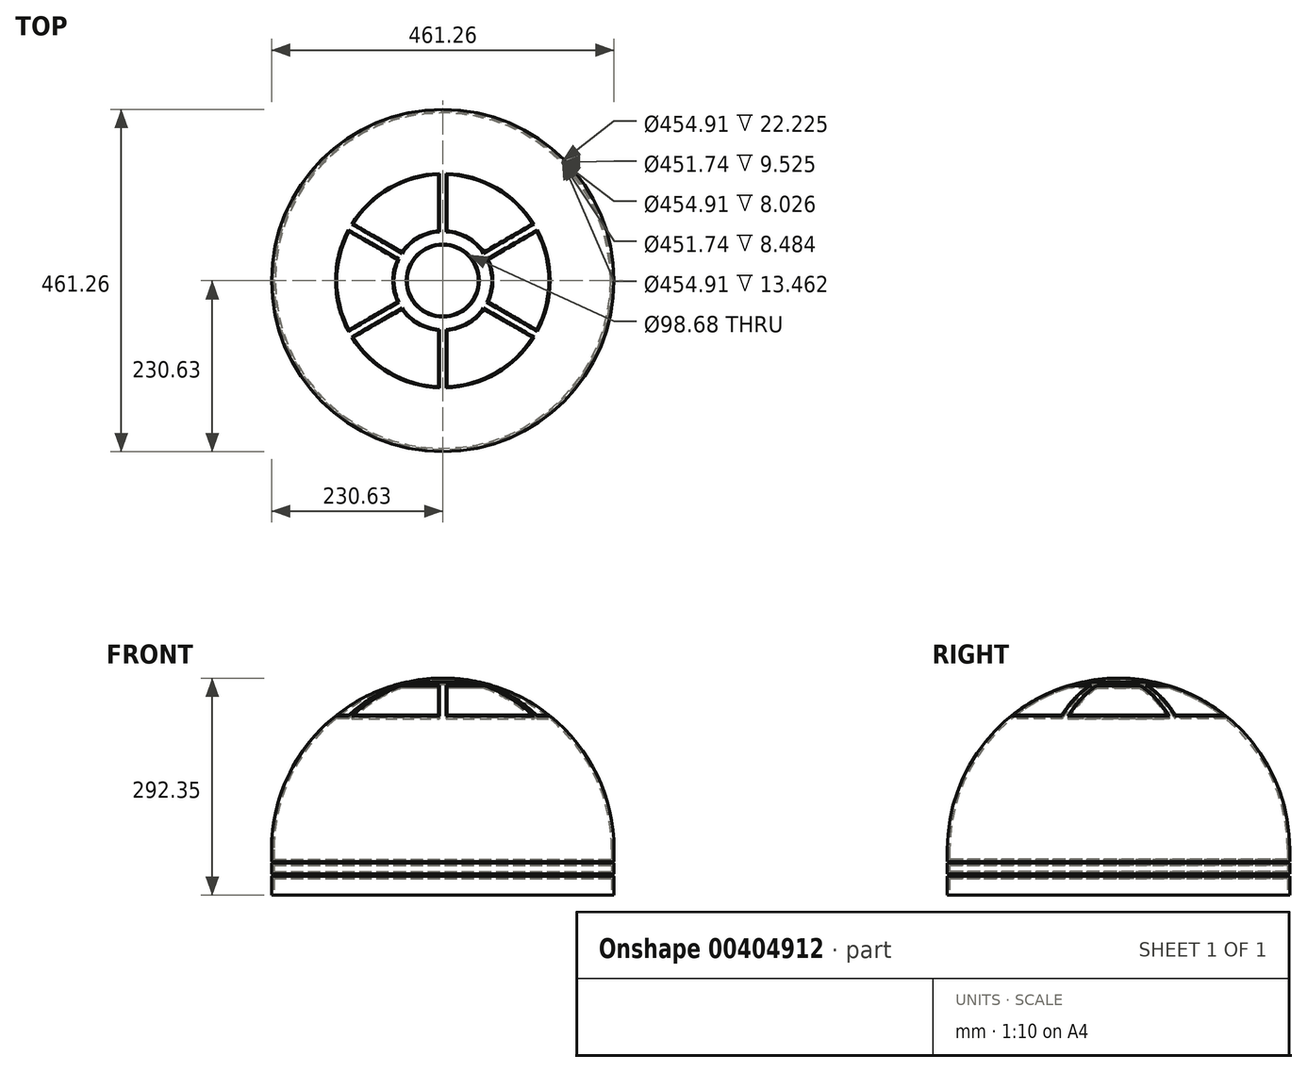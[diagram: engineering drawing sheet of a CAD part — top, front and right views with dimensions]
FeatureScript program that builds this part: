
annotation { "Feature Type Name" : "Feature", "Feature Type Description" : "" }
export const myFeature = defineFeature(function(context is Context, id is Id, definition is map)
    precondition{}
    {
        {
            var Q0;
            Q0=qCreatedBy(makeId("Front.planeOp"),FACE);
            var sketch = newSketch(context, id + "F0", { "sketchPlane" : qUnion([Q0])});
            skLineSegment(sketch, "E0", {"start": v(0, 0) * mm, "end": v(230.63, 0) * mm, "construction": true});
            skLineSegment(sketch, "E1", {"start": v(0, 0) * mm, "end": v(0, 230.63) * mm});
            skArc(sketch, "E2", {"start": v(0, 230.63) * mm, "mid": v(163.08, 163.08) * mm, "end": v(230.63, 0) * mm});
            skLineSegment(sketch, "E3.0", {"start": v(0, -61.72) * mm, "end": v(230.63, -61.72) * mm});
            skLineSegment(sketch, "E4", {"start": v(230.63, 0) * mm, "end": v(230.63, -61.72) * mm});
            skLineSegment(sketch, "E5", {"start": v(0, 0) * mm, "end": v(0, -61.72) * mm});
            skLineSegment(sketch, "E6", {"start": v(0, -16.64) * mm, "end": v(255.24, -16.64) * mm, "construction": true});
            skLineSegment(sketch, "E7", {"start": v(0, -11.56) * mm, "end": v(242.63, -11.56) * mm, "construction": true});
            skLineSegment(sketch, "E8", {"start": v(0, 67.06) * mm, "end": v(239.12, 67.06) * mm, "construction": true});
            skLineSegment(sketch, "E9", {"start": v(0, -36.32) * mm, "end": v(246, -36.32) * mm, "construction": true});
            skLineSegment(sketch, "E10", {"start": v(0, 179.58) * mm, "end": v(247.78, 179.58) * mm, "construction": true});
            skLineSegment(sketch, "E11", {"start": v(0, 219.96) * mm, "end": v(197.7, 219.96) * mm, "construction": true});
            skLineSegment(sketch, "E12", {"start": v(0, 224.97) * mm, "end": v(99.38, 224.97) * mm, "construction": true});
            skSolve(sketch);
        }
        {
            var Q0;
            Q0 = qSketchRegion(id + "F0", true);
            var Q1;
            Q1=sQuery(id+"F0.wireOp",EDGE,"E1");
            revolve(context, id + "F1", {"surfaceOperationType" : NewSurfaceOperationType.NEW, "entities" : qUnion([Q0]), "axis" : qUnion([Q1]), "revolveType" : RevolveType.FULL});
        }
        {
            var Q0;
            Q0=qCreatedBy(makeId("Front.planeOp"),FACE);
            var sketch = newSketch(context, id + "F2", { "sketchPlane" : qUnion([Q0])});
            skLineSegment(sketch, "E13.bottom", {"start": v(230.63, -33.15) * mm, "end": v(229.04, -33.15) * mm});
            skLineSegment(sketch, "E13.top", {"start": v(230.63, -36.32) * mm, "end": v(229.04, -36.32) * mm});
            skLineSegment(sketch, "E13.left", {"start": v(230.63, -33.15) * mm, "end": v(230.63, -36.32) * mm});
            skLineSegment(sketch, "E13.right", {"start": v(229.04, -33.15) * mm, "end": v(229.04, -36.32) * mm});
            skLineSegment(sketch, "E14.bottom", {"start": v(230.63, -16.64) * mm, "end": v(229.04, -16.64) * mm});
            skLineSegment(sketch, "E14.top", {"start": v(230.63, -18.77) * mm, "end": v(229.04, -18.77) * mm});
            skLineSegment(sketch, "E14.left", {"start": v(230.63, -16.64) * mm, "end": v(230.63, -18.77) * mm});
            skLineSegment(sketch, "E14.right", {"start": v(229.04, -16.64) * mm, "end": v(229.04, -18.77) * mm});
            skLineSegment(sketch, "E15", {"start": v(0, 0) * mm, "end": v(0, -62.1) * mm, "construction": true});
            skSolve(sketch);
        }
        {
            var Q0;
            Q0 = qSketchRegion(id + "F2", true);
            var Q1;
            Q1=sQuery(id+"F0.wireOp",EDGE,"E5");
            revolve(context, id + "F3", {"operationType" : NewBodyOperationType.REMOVE, "entities" : qUnion([Q0]), "axis" : qUnion([Q1]), "revolveType" : RevolveType.FULL});
        }
        {
            var Q0;
            Q0=qCreatedBy(makeId("Top.planeOp"),FACE);
            var sketch = newSketch(context, id + "F4", { "sketchPlane" : qUnion([Q0])});
            skArc(sketch, "E16", {"start": v(4.36, -144.4) * mm, "mid": v(72.23, -125.1) * mm, "end": v(122.87, -75.97) * mm});
            skArc(sketch, "E17", {"start": v(4.36, -65.67) * mm, "mid": v(32.9, -57) * mm, "end": v(54.7, -36.6) * mm});
            skCircle(sketch, "E18", {"center": v(0, 0) * mm, "radius": 49.34 * mm});
            skLineSegment(sketch, "E19", {"start": v(0, 0) * mm, "end": v(0, -49.34) * mm, "construction": true});
            skLineSegment(sketch, "E20.trimOffspring", {"start": v(4.36, -65.67) * mm, "end": v(4.36, -144.4) * mm});
            skLineSegment(sketch, "E21.trimOffspring", {"start": v(0, -65.81) * mm, "end": v(0, -144.46) * mm, "construction": true});
            skLineSegment(sketch, "E22.1.1", {"start": v(54.7, -36.6) * mm, "end": v(122.87, -75.97) * mm});
            skLineSegment(sketch, "E23.0", {"start": v(5.94, -67.14) * mm, "end": v(5.94, -142.75) * mm});
            skArc(sketch, "E23.1", {"start": v(5.94, -67.14) * mm, "mid": v(33.7, -58.37) * mm, "end": v(55.17, -38.72) * mm});
            skLineSegment(sketch, "E23.2", {"start": v(55.17, -38.72) * mm, "end": v(120.65, -76.52) * mm});
            skArc(sketch, "E23.3", {"start": v(5.94, -142.75) * mm, "mid": v(71.44, -123.73) * mm, "end": v(120.65, -76.52) * mm});
            skArc(sketch, "E24.1.0", {"start": v(126.6, -66.23) * mm, "mid": v(142.88, 0) * mm, "end": v(126.6, 66.23) * mm});
            skLineSegment(sketch, "E24.1.1", {"start": v(59.05, -29.06) * mm, "end": v(127.23, -68.43) * mm});
            skArc(sketch, "E24.1.2", {"start": v(59.05, -29.06) * mm, "mid": v(65.81, 0) * mm, "end": v(59.05, 29.06) * mm});
            skLineSegment(sketch, "E24.1.3", {"start": v(61.11, -28.42) * mm, "end": v(126.6, -66.23) * mm});
            skArc(sketch, "E24.1.4", {"start": v(61.11, -28.42) * mm, "mid": v(67.4, 0) * mm, "end": v(61.11, 28.42) * mm});
            skArc(sketch, "E24.1.5", {"start": v(127.23, -68.43) * mm, "mid": v(144.46, 0) * mm, "end": v(127.23, 68.43) * mm});
            skLineSegment(sketch, "E24.1.6", {"start": v(61.11, 28.42) * mm, "end": v(126.6, 66.23) * mm});
            skLineSegment(sketch, "E24.1.7", {"start": v(59.05, 29.06) * mm, "end": v(127.23, 68.43) * mm});
            skArc(sketch, "E24.2.0", {"start": v(120.65, 76.52) * mm, "mid": v(71.44, 123.73) * mm, "end": v(5.94, 142.75) * mm});
            skLineSegment(sketch, "E24.2.1", {"start": v(54.7, 36.6) * mm, "end": v(122.87, 75.97) * mm});
            skArc(sketch, "E24.2.2", {"start": v(54.7, 36.6) * mm, "mid": v(32.9, 57) * mm, "end": v(4.36, 65.67) * mm});
            skLineSegment(sketch, "E24.2.3", {"start": v(55.17, 38.72) * mm, "end": v(120.65, 76.52) * mm});
            skArc(sketch, "E24.2.4", {"start": v(55.17, 38.72) * mm, "mid": v(33.7, 58.37) * mm, "end": v(5.94, 67.14) * mm});
            skArc(sketch, "E24.2.5", {"start": v(122.87, 75.97) * mm, "mid": v(72.23, 125.1) * mm, "end": v(4.36, 144.4) * mm});
            skLineSegment(sketch, "E24.2.6", {"start": v(5.94, 67.14) * mm, "end": v(5.94, 142.75) * mm});
            skLineSegment(sketch, "E24.2.7", {"start": v(4.36, 65.67) * mm, "end": v(4.36, 144.4) * mm});
            skArc(sketch, "E24.3.0", {"start": v(-5.94, 142.75) * mm, "mid": v(-71.44, 123.73) * mm, "end": v(-120.65, 76.52) * mm});
            skLineSegment(sketch, "E24.3.1", {"start": v(-4.36, 65.67) * mm, "end": v(-4.36, 144.4) * mm});
            skArc(sketch, "E24.3.2", {"start": v(-4.36, 65.67) * mm, "mid": v(-32.9, 57) * mm, "end": v(-54.7, 36.6) * mm});
            skLineSegment(sketch, "E24.3.3", {"start": v(-5.94, 67.14) * mm, "end": v(-5.94, 142.75) * mm});
            skArc(sketch, "E24.3.4", {"start": v(-5.94, 67.14) * mm, "mid": v(-33.7, 58.37) * mm, "end": v(-55.17, 38.72) * mm});
            skArc(sketch, "E24.3.5", {"start": v(-4.36, 144.4) * mm, "mid": v(-72.23, 125.1) * mm, "end": v(-122.87, 75.97) * mm});
            skLineSegment(sketch, "E24.3.6", {"start": v(-55.17, 38.72) * mm, "end": v(-120.65, 76.52) * mm});
            skLineSegment(sketch, "E24.3.7", {"start": v(-54.7, 36.6) * mm, "end": v(-122.87, 75.97) * mm});
            skArc(sketch, "E24.4.0", {"start": v(-126.6, 66.23) * mm, "mid": v(-142.88, 0) * mm, "end": v(-126.6, -66.23) * mm});
            skLineSegment(sketch, "E24.4.1", {"start": v(-59.05, 29.06) * mm, "end": v(-127.23, 68.43) * mm});
            skArc(sketch, "E24.4.2", {"start": v(-59.05, 29.06) * mm, "mid": v(-65.81, 0) * mm, "end": v(-59.05, -29.06) * mm});
            skLineSegment(sketch, "E24.4.3", {"start": v(-61.11, 28.42) * mm, "end": v(-126.6, 66.23) * mm});
            skArc(sketch, "E24.4.4", {"start": v(-61.11, 28.42) * mm, "mid": v(-67.4, 0) * mm, "end": v(-61.11, -28.42) * mm});
            skArc(sketch, "E24.4.5", {"start": v(-127.23, 68.43) * mm, "mid": v(-144.46, 0) * mm, "end": v(-127.23, -68.43) * mm});
            skLineSegment(sketch, "E24.4.6", {"start": v(-61.11, -28.42) * mm, "end": v(-126.6, -66.23) * mm});
            skLineSegment(sketch, "E24.4.7", {"start": v(-59.05, -29.06) * mm, "end": v(-127.23, -68.43) * mm});
            skArc(sketch, "E24.5.0", {"start": v(-120.65, -76.52) * mm, "mid": v(-71.44, -123.73) * mm, "end": v(-5.94, -142.75) * mm});
            skLineSegment(sketch, "E24.5.1", {"start": v(-54.7, -36.6) * mm, "end": v(-122.87, -75.97) * mm});
            skArc(sketch, "E24.5.2", {"start": v(-54.7, -36.6) * mm, "mid": v(-32.9, -57) * mm, "end": v(-4.36, -65.67) * mm});
            skLineSegment(sketch, "E24.5.3", {"start": v(-55.17, -38.72) * mm, "end": v(-120.65, -76.52) * mm});
            skArc(sketch, "E24.5.4", {"start": v(-55.17, -38.72) * mm, "mid": v(-33.7, -58.37) * mm, "end": v(-5.94, -67.14) * mm});
            skArc(sketch, "E24.5.5", {"start": v(-122.87, -75.97) * mm, "mid": v(-72.23, -125.1) * mm, "end": v(-4.36, -144.4) * mm});
            skLineSegment(sketch, "E24.5.6", {"start": v(-5.94, -67.14) * mm, "end": v(-5.94, -142.75) * mm});
            skLineSegment(sketch, "E24.5.7", {"start": v(-4.36, -65.67) * mm, "end": v(-4.36, -144.4) * mm});
            skCircle(sketch, "E25.0", {"center": v(0, 0) * mm, "radius": 47.75 * mm});
            skSolve(sketch);
        }
        {
            var Q0;
            Q0=makeQuery(id+"F1.opRevolve","SWEPT_FACE",FACE,{"disambiguationData":[OSD([sQuery(id+"F0.wireOp",EDGE,"E3.0")])]});
            shell(context, id + "F5", {"entities" : qUnion([Q0]), "thickness" : 3.17 * mm});
        }
        {
            var Q0;
            Q0=makeQuery(id+"F4.imprint","IMPRINT",FACE,{"disambiguationData":[TD([[makeQuery(id+"F4.imprint","IMPRINT",EDGE,{"derivedFrom":sQuery(id+"F4.wireOp",EDGE,"E24.4.0")}),-1.0]])]});
            var Q1;
            Q1=makeQuery(id+"F4.imprint","IMPRINT",FACE,{"disambiguationData":[TD([[makeQuery(id+"F4.imprint","IMPRINT",EDGE,{"derivedFrom":sQuery(id+"F4.wireOp",EDGE,"E24.3.0")}),-1.0]])]});
            var Q2;
            Q2=makeQuery(id+"F4.imprint","IMPRINT",FACE,{"disambiguationData":[TD([[makeQuery(id+"F4.imprint","IMPRINT",EDGE,{"derivedFrom":sQuery(id+"F4.wireOp",EDGE,"E18")}),1.0]])]});
            var Q3;
            Q3=makeQuery(id+"F4.imprint","IMPRINT",FACE,{"disambiguationData":[TD([[makeQuery(id+"F4.imprint","IMPRINT",EDGE,{"derivedFrom":sQuery(id+"F4.wireOp",EDGE,"E24.2.0")}),-1.0]])]});
            var Q4;
            Q4=makeQuery(id+"F4.imprint","IMPRINT",FACE,{"disambiguationData":[TD([[makeQuery(id+"F4.imprint","IMPRINT",EDGE,{"derivedFrom":sQuery(id+"F4.wireOp",EDGE,"E24.1.0")}),-1.0]])]});
            var Q5;
            Q5=makeQuery(id+"F4.imprint","IMPRINT",FACE,{"disambiguationData":[TD([[makeQuery(id+"F4.imprint","IMPRINT",EDGE,{"derivedFrom":sQuery(id+"F4.wireOp",EDGE,"E16")}),1.0]])]});
            var Q6;
            Q6=makeQuery(id+"F4.imprint","IMPRINT",FACE,{"disambiguationData":[TD([[makeQuery(id+"F4.imprint","IMPRINT",EDGE,{"derivedFrom":sQuery(id+"F4.wireOp",EDGE,"E24.5.0")}),-1.0]])]});
            extrude(context, id + "F6", {"entities" : qUnion([Q0, Q1, Q2, Q3, Q4, Q5, Q6]), "operationType" : NewBodyOperationType.REMOVE, "endBound" : BoundingType.THROUGH_ALL, "depth" : 25.4 * mm, "hasSecondDirection" : true, "secondDirectionBound" : SecondDirectionBoundingType.THROUGH_ALL, "secondDirectionOppositeDirection" : true, "secondDirectionDepth" : 25.4 * mm});
        }
    });
